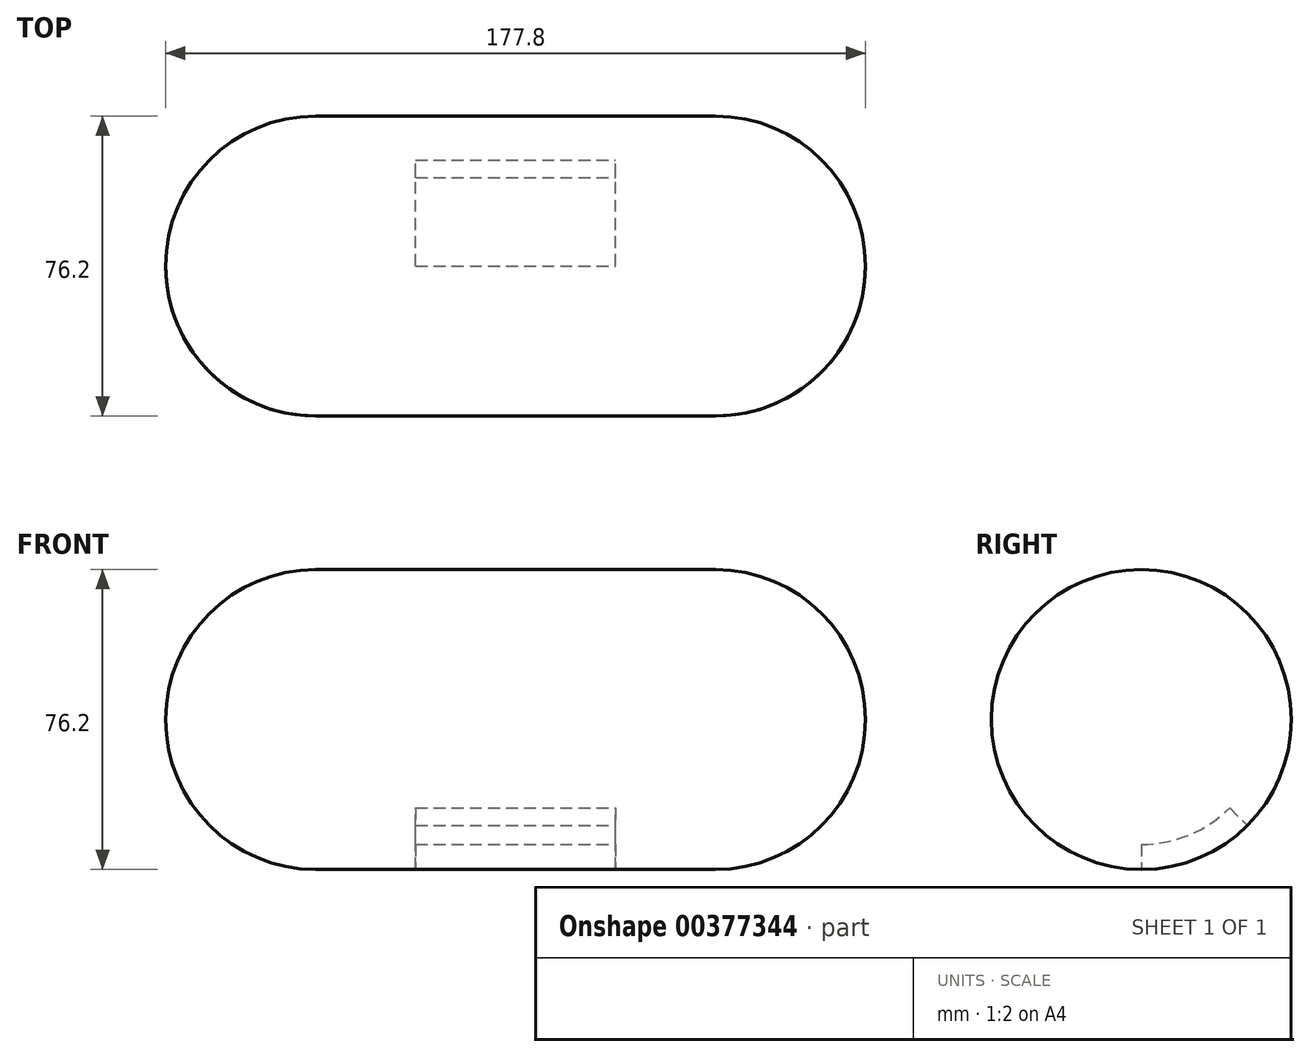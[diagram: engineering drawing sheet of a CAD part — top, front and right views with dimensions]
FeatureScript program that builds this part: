
annotation { "Feature Type Name" : "Feature", "Feature Type Description" : "" }
export const myFeature = defineFeature(function(context is Context, id is Id, definition is map)
    precondition{}
    {
        {
            var Q0;
            Q0=qCreatedBy(makeId("Top.planeOp"),FACE);
            var sketch = newSketch(context, id + "F0", { "sketchPlane" : qUnion([Q0])});
            skLineSegment(sketch, "E0.bottom", {"start": v(-50.8, 36.78) * mm, "end": v(50.8, 36.78) * mm});
            skLineSegment(sketch, "E0.top", {"start": v(-50.8, -39.42) * mm, "end": v(50.8, -39.42) * mm});
            skLineSegment(sketch, "E0.left", {"start": v(-50.8, 36.78) * mm, "end": v(-50.8, -39.42) * mm});
            skLineSegment(sketch, "E0.right", {"start": v(50.8, 36.78) * mm, "end": v(50.8, -39.42) * mm});
            skArc(sketch, "E1", {"start": v(-50.8, 36.78) * mm, "mid": v(-88.9, -1.32) * mm, "end": v(-50.8, -39.42) * mm});
            skArc(sketch, "E2", {"start": v(50.8, -39.42) * mm, "mid": v(88.9, -1.32) * mm, "end": v(50.8, 36.78) * mm});
            skLineSegment(sketch, "E3", {"start": v(-50.8, -1.32) * mm, "end": v(50.8, -1.32) * mm});
            skLineSegment(sketch, "E4", {"start": v(-50.8, -1.32) * mm, "end": v(-88.9, -1.32) * mm});
            skLineSegment(sketch, "E5", {"start": v(50.8, -1.32) * mm, "end": v(88.9, -1.32) * mm});
            skLineSegment(sketch, "E6", {"start": v(0, -39.42) * mm, "end": v(0, -1.32) * mm});
            skSolve(sketch);
        }
        {
            var Q0;
            {var subQ3=sQuery(id+"F0.wireOp",EDGE,"E5");Q0=makeQuery(id+"F0.imprint","IMPRINT",FACE,{"disambiguationData":[TD([[makeQuery(id+"F0.imprint","IMPRINT",EDGE,{"derivedFrom":subQ3}),-1.0]])]});}
            var Q1;
            {var subQ0=sQuery(id+"F0.wireOp",EDGE,"E0.top");Q1=makeQuery(id+"F0.imprint","IMPRINT",FACE,{"disambiguationData":[TD([[makeQuery(id+"F0.imprint","IMPRINT",EDGE,{"derivedFrom":subQ0}),1.0]])]});}
            var Q2;
            {var subQ3=sQuery(id+"F0.wireOp",EDGE,"E4");Q2=makeQuery(id+"F0.imprint","IMPRINT",FACE,{"disambiguationData":[TD([[makeQuery(id+"F0.imprint","IMPRINT",EDGE,{"derivedFrom":subQ3}),1.0]])]});}
            var Q3;
            Q3=sQuery(id+"F0.wireOp",EDGE,"E3");
            revolve(context, id + "F1", {"entities" : qUnion([Q0, Q1, Q2]), "axis" : qUnion([Q3]), "revolveType" : RevolveType.FULL});
        }
        {
            var Q0;
            Q0=qCreatedBy(makeId("Right.planeOp"),FACE);
            var sketch = newSketch(context, id + "F2", { "sketchPlane" : qUnion([Q0])});
            skCircle(sketch, "E7.0", {"center": v(-1.32, 0) * mm, "radius": 38.1 * mm});
            skLineSegment(sketch, "E8", {"start": v(-28.26, -26.94) * mm, "end": v(-23.77, -22.45) * mm});
            skCircle(sketch, "E9", {"center": v(-1.32, 0) * mm, "radius": 31.75 * mm});
            skLineSegment(sketch, "E10", {"start": v(-1.32, 0) * mm, "end": v(-1.32, -38.1) * mm});
            skLineSegment(sketch, "E11", {"start": v(-1.32, 0) * mm, "end": v(25.62, -26.94) * mm});
            skSolve(sketch);
        }
        {
            var Q0;
            {var subQ0=sQuery(id+"F2.wireOp",EDGE,"E10");var subQ1=sQuery(id+"F2.wireOp",EDGE,"E7.0");var subQ2=makeQuery(id+"F2.imprint","INTERSECT",VERTEX,{"derivedFrom":[subQ1,subQ0]});Q0=makeQuery(id+"F2.imprint","IMPRINT",FACE,{"disambiguationData":[TD([[makeQuery(id+"F2.imprint","IMPRINT",EDGE,{"disambiguationData":[TD([[subQ2,-1.0]])],"derivedFrom":subQ1}),1.0]])]});}
            extrude(context, id + "F3", {"entities" : qUnion([Q0]), "operationType" : NewBodyOperationType.REMOVE, "endBound" : BoundingType.SYMMETRIC, "oppositeDirection" : true, "depth" : 50.8 * mm});
        }
    });
